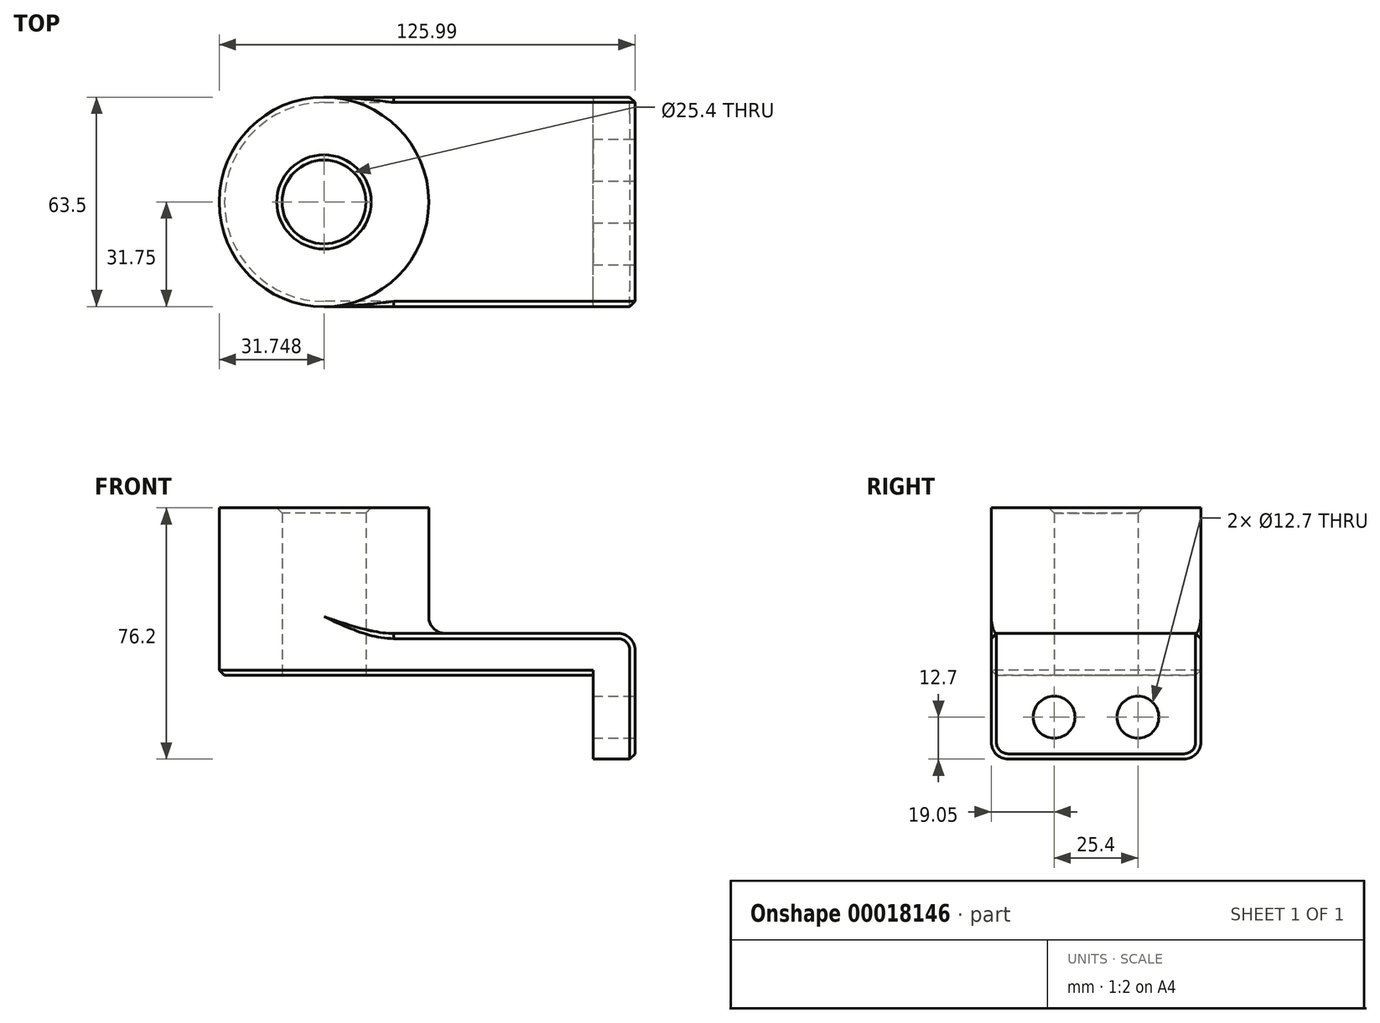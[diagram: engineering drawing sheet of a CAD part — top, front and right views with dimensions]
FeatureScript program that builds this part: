
annotation { "Feature Type Name" : "Feature", "Feature Type Description" : "" }
export const myFeature = defineFeature(function(context is Context, id is Id, definition is map)
    precondition{}
    {
        {
            var Q0;
            Q0=qCreatedBy(makeId("Top.planeOp"),FACE);
            var sketch = newSketch(context, id + "F0", { "sketchPlane" : qUnion([Q0])});
            skLineSegment(sketch, "E0.rect.bottom", {"start": v(47.12, 31.75) * mm, "end": v(-47.12, 31.75) * mm});
            skLineSegment(sketch, "E0.rect.top", {"start": v(47.12, -31.75) * mm, "end": v(-47.12, -31.75) * mm});
            skLineSegment(sketch, "E0.rect.left", {"start": v(47.12, 31.75) * mm, "end": v(47.12, -31.75) * mm});
            skLineSegment(sketch, "E0.rect.right", {"start": v(-47.12, 31.75) * mm, "end": v(-47.12, -31.75) * mm});
            skPoint(sketch, "E0.rect.middle", {"position": v(0, 0) * mm});
            skCircle(sketch, "E1", {"center": v(-47.12, 0) * mm, "radius": 31.75 * mm});
            skCircle(sketch, "E2", {"center": v(-47.12, 0) * mm, "radius": 12.7 * mm});
            skSolve(sketch);
        }
        {
            var Q0;
            {var subQ3=sQuery(id+"F0.wireOp",EDGE,"E0.rect.bottom");Q0=makeQuery(id+"F0.imprint","IMPRINT",FACE,{"disambiguationData":[TD([[makeQuery(id+"F0.imprint","IMPRINT",EDGE,{"derivedFrom":subQ3}),1.0]])]});}
            var Q1;
            {var subQ0=sQuery(id+"F0.wireOp",EDGE,"E2");var subQ1=sQuery(id+"F0.wireOp",EDGE,"E0.rect.right");var subQ3=makeQuery(id+"F0.imprint","INTERSECT",VERTEX,{"disambiguationData":[OD(0.0)],"derivedFrom":[subQ1,subQ0]});Q1=makeQuery(id+"F0.imprint","IMPRINT",FACE,{"disambiguationData":[TD([[makeQuery(id+"F0.imprint","IMPRINT",EDGE,{"disambiguationData":[TD([[subQ3,-1.0]])],"derivedFrom":subQ0}),-1.0]])]});}
            var Q2;
            {var subQ0=sQuery(id+"F0.wireOp",EDGE,"E2");var subQ1=sQuery(id+"F0.wireOp",EDGE,"E0.rect.right");var subQ3=makeQuery(id+"F0.imprint","INTERSECT",VERTEX,{"disambiguationData":[OD(0.0)],"derivedFrom":[subQ1,subQ0]});Q2=makeQuery(id+"F0.imprint","IMPRINT",FACE,{"disambiguationData":[TD([[makeQuery(id+"F0.imprint","IMPRINT",EDGE,{"disambiguationData":[TD([[subQ3,1.0]])],"derivedFrom":subQ0}),-1.0]])]});}
            extrude(context, id + "F1", {"entities" : qUnion([Q0, Q1, Q2]), "depth" : 12.7 * mm});
        }
        {
            var Q0;
            {var subQ0=sQuery(id+"F0.wireOp",EDGE,"E2");var subQ1=sQuery(id+"F0.wireOp",EDGE,"E0.rect.right");var subQ3=makeQuery(id+"F0.imprint","INTERSECT",VERTEX,{"disambiguationData":[OD(0.0)],"derivedFrom":[subQ1,subQ0]});Q0=makeQuery(id+"F0.imprint","IMPRINT",FACE,{"disambiguationData":[TD([[makeQuery(id+"F0.imprint","IMPRINT",EDGE,{"disambiguationData":[TD([[subQ3,-1.0]])],"derivedFrom":subQ0}),-1.0]])]});}
            var Q1;
            {var subQ0=sQuery(id+"F0.wireOp",EDGE,"E2");var subQ1=sQuery(id+"F0.wireOp",EDGE,"E0.rect.right");var subQ3=makeQuery(id+"F0.imprint","INTERSECT",VERTEX,{"disambiguationData":[OD(0.0)],"derivedFrom":[subQ1,subQ0]});Q1=makeQuery(id+"F0.imprint","IMPRINT",FACE,{"disambiguationData":[TD([[makeQuery(id+"F0.imprint","IMPRINT",EDGE,{"disambiguationData":[TD([[subQ3,1.0]])],"derivedFrom":subQ0}),-1.0]])]});}
            extrude(context, id + "F2", {"entities" : qUnion([Q0, Q1]), "operationType" : NewBodyOperationType.ADD, "depth" : 50.8 * mm});
        }
        {
            var Q0;
            Q0=makeQuery(id+"F1.opExtrude","SWEPT_FACE",FACE,{"disambiguationData":[OSD([sQuery(id+"F0.wireOp",EDGE,"E0.rect.left")])]});
            var sketch = newSketch(context, id + "F3", { "sketchPlane" : qUnion([Q0])});
            skLineSegment(sketch, "E3.bottom", {"start": v(-31.75, 12.7) * mm, "end": v(31.75, 12.7) * mm});
            skLineSegment(sketch, "E3.top", {"start": v(-31.75, -25.4) * mm, "end": v(31.75, -25.4) * mm});
            skLineSegment(sketch, "E3.left", {"start": v(-31.75, 12.7) * mm, "end": v(-31.75, -25.4) * mm});
            skLineSegment(sketch, "E3.right", {"start": v(31.75, 12.7) * mm, "end": v(31.75, -25.4) * mm});
            skCircle(sketch, "E4", {"center": v(-12.7, -12.7) * mm, "radius": 6.35 * mm});
            skLineSegment(sketch, "E5", {"start": v(0, 0) * mm, "end": v(0, -25.4) * mm});
            skCircle(sketch, "E6.MirrorC", {"center": v(12.7, -12.7) * mm, "radius": 6.35 * mm});
            skSolve(sketch);
        }
        {
            var Q0;
            Q0 = qSketchRegion(id + "F3", true);
            extrude(context, id + "F4", {"entities" : qUnion([Q0]), "operationType" : NewBodyOperationType.ADD, "oppositeDirection" : true, "depth" : 12.7 * mm});
        }
        {
            var Q0;
            {var subQ0=sQuery(id+"F0.wireOp",EDGE,"E1");Q0=makeQuery(id+"F2.boolean.opBoolean","INTERSECT",EDGE,{"derivedFrom":[makeQuery(id+"F1.opExtrude","CAP_FACE",FACE,{"disambiguationData":[OSD([sQuery(id+"F0.wireOp",EDGE,"E0.rect.bottom"),sQuery(id+"F0.wireOp",EDGE,"E0.rect.top"),sQuery(id+"F0.wireOp",EDGE,"E0.rect.left"),subQ0,sQuery(id+"F0.wireOp",EDGE,"E2")])],"isStart":false}),makeQuery(id+"F2.opExtrude","SWEPT_FACE",FACE,{"disambiguationData":[OSD([subQ0])]})]});}
            var Q1;
            Q1=makeQuery(id+"F1.opExtrude","CAP_EDGE",EDGE,{"disambiguationData":[OSD([sQuery(id+"F0.wireOp",EDGE,"E0.rect.left")])],"isStart":false});
            var Q2;
            Q2=makeQuery(id+"F4.opExtrude","SWEPT_EDGE",EDGE,{"disambiguationData":[OSD([sQuery(id+"F3.wireOp",EDGE,"E3.top"),sQuery(id+"F3.wireOp",EDGE,"E3.left")])]});
            var Q3;
            Q3=makeQuery(id+"F4.opExtrude","SWEPT_EDGE",EDGE,{"disambiguationData":[OSD([sQuery(id+"F3.wireOp",EDGE,"E3.top"),sQuery(id+"F3.wireOp",EDGE,"E3.right")])]});
            fillet(context, id + "F5", {"entities" : qUnion([Q0, Q1, Q2, Q3]), "radius" : 5.08 * mm, "tangentPropagation" : true, "allowEdgeOverflow" : false});
        }
        {
            var Q0;
            Q0=makeQuery(id+"F1.opExtrude","CAP_EDGE",EDGE,{"disambiguationData":[OSD([sQuery(id+"F0.wireOp",EDGE,"E0.rect.bottom")])],"isStart":false});
            var Q1;
            Q1=makeQuery(id+"F1.opExtrude","CAP_EDGE",EDGE,{"disambiguationData":[OSD([sQuery(id+"F0.wireOp",EDGE,"E0.rect.bottom")])],"isStart":true});
            var Q2;
            Q2=makeQuery(id+"F2.opExtrude","CAP_EDGE",EDGE,{"disambiguationData":[OSD([sQuery(id+"F0.wireOp",EDGE,"E2")])],"isStart":false});
            chamfer(context, id + "F6", {"entities" : qUnion([Q0, Q1, Q2]), "width" : 1.59 * mm, "tangentPropagation" : true});
        }
    });
